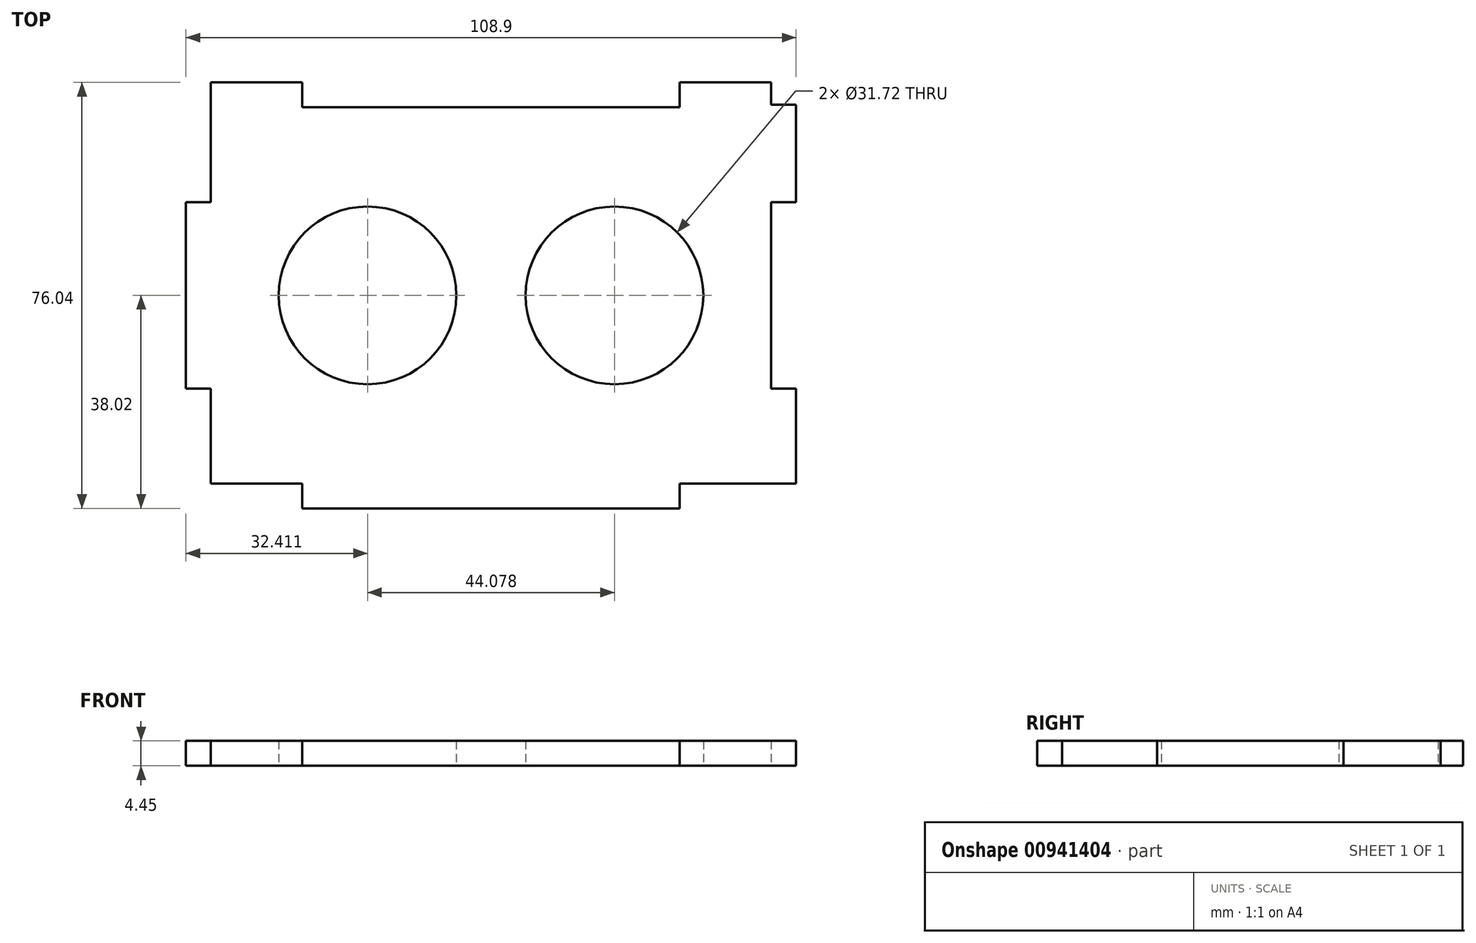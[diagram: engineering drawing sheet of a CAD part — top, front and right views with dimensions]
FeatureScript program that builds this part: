
annotation { "Feature Type Name" : "Feature", "Feature Type Description" : "" }
export const myFeature = defineFeature(function(context is Context, id is Id, definition is map)
    precondition{}
    {
        {
            var Q0;
            Q0=qCreatedBy(makeId("Top.planeOp"),FACE);
            var sketch = newSketch(context, id + "F0", { "sketchPlane" : qUnion([Q0])});
            skLineSegment(sketch, "E0.bottom", {"start": v(50, -33.57) * mm, "end": v(33.7, -33.57) * mm});
            skLineSegment(sketch, "E0.top", {"start": v(33.7, 33.57) * mm, "end": v(-33.7, 33.57) * mm});
            skLineSegment(sketch, "E0.left", {"start": v(50, -16.64) * mm, "end": v(50, 16.64) * mm});
            skLineSegment(sketch, "E0.right", {"start": v(-50, -33.57) * mm, "end": v(-50, -16.64) * mm});
            skPoint(sketch, "E0.middle", {"position": v(0, 0) * mm});
            skLineSegment(sketch, "E1.top", {"start": v(-50, 38.02) * mm, "end": v(-33.7, 38.02) * mm});
            skLineSegment(sketch, "E1.left", {"start": v(-50, 33.57) * mm, "end": v(-50, 38.02) * mm});
            skLineSegment(sketch, "E1.right", {"start": v(-33.7, 33.57) * mm, "end": v(-33.7, 38.02) * mm});
            skLineSegment(sketch, "E2.MirrorCS", {"start": v(50, 38.02) * mm, "end": v(33.7, 38.02) * mm});
            skLineSegment(sketch, "E3.MirrorCS", {"start": v(33.7, 33.57) * mm, "end": v(33.7, 38.02) * mm});
            skLineSegment(sketch, "E4.MirrorCS", {"start": v(50, 33.57) * mm, "end": v(50, 38.02) * mm});
            skLineSegment(sketch, "E5.top", {"start": v(-33.7, -38.02) * mm, "end": v(33.7, -38.02) * mm});
            skLineSegment(sketch, "E5.left", {"start": v(-33.7, -33.57) * mm, "end": v(-33.7, -38.02) * mm});
            skLineSegment(sketch, "E5.right", {"start": v(33.7, -33.57) * mm, "end": v(33.7, -38.02) * mm});
            skLineSegment(sketch, "E6.bottom", {"start": v(-50, -16.64) * mm, "end": v(-54.45, -16.64) * mm});
            skLineSegment(sketch, "E6.top", {"start": v(-50, 16.64) * mm, "end": v(-54.45, 16.64) * mm});
            skLineSegment(sketch, "E6.right", {"start": v(-54.45, -16.64) * mm, "end": v(-54.45, 16.64) * mm});
            skPoint(sketch, "E6.middle", {"position": v(-50, 0) * mm});
            skPoint(sketch, "E7.orphan", {"position": v(-45.55, 16.64) * mm});
            skPoint(sketch, "E8.orphan", {"position": v(-45.55, -16.64) * mm});
            skLineSegment(sketch, "E9.bottom", {"start": v(50, 16.64) * mm, "end": v(54.45, 16.64) * mm});
            skLineSegment(sketch, "E9.top", {"start": v(50, 34) * mm, "end": v(54.45, 34) * mm});
            skLineSegment(sketch, "E9.left", {"start": v(50, 33.57) * mm, "end": v(50, 34) * mm});
            skLineSegment(sketch, "E9.right", {"start": v(54.45, 16.64) * mm, "end": v(54.45, 34) * mm});
            skLineSegment(sketch, "E10.MirrorCS", {"start": v(54.45, -16.64) * mm, "end": v(54.45, -33.57) * mm});
            skLineSegment(sketch, "E11.MirrorCS", {"start": v(50, -16.64) * mm, "end": v(54.45, -16.64) * mm});
            skLineSegment(sketch, "E12", {"start": v(50, -33.57) * mm, "end": v(54.45, -33.57) * mm});
            skPoint(sketch, "E13.MirrorCS.end.orphan", {"position": v(54.45, -34) * mm});
            skPoint(sketch, "E13.MirrorCS.start.orphan", {"position": v(50, -34) * mm});
            skLineSegment(sketch, "E14.trimOffspring", {"start": v(-33.7, -33.57) * mm, "end": v(-50, -33.57) * mm});
            skLineSegment(sketch, "E15.trimOffspring", {"start": v(-50, 16.64) * mm, "end": v(-50, 33.57) * mm});
            skCircle(sketch, "E16", {"center": v(-22.04, 0) * mm, "radius": 15.86 * mm});
            skCircle(sketch, "E17.MirrorC", {"center": v(22.04, 0) * mm, "radius": 15.86 * mm});
            skSolve(sketch);
        }
        {
            var Q0;
            Q0=makeQuery(id+"F0.imprint","IMPRINT",FACE,{"disambiguationData":[TD([[makeQuery(id+"F0.imprint","IMPRINT",EDGE,{"derivedFrom":sQuery(id+"F0.wireOp",EDGE,"E0.bottom")}),-1.0]])]});
            extrude(context, id + "F1", {"entities" : qUnion([Q0]), "depth" : 4.45 * mm, "offsetDistance" : 25 * mm});
        }
    });
